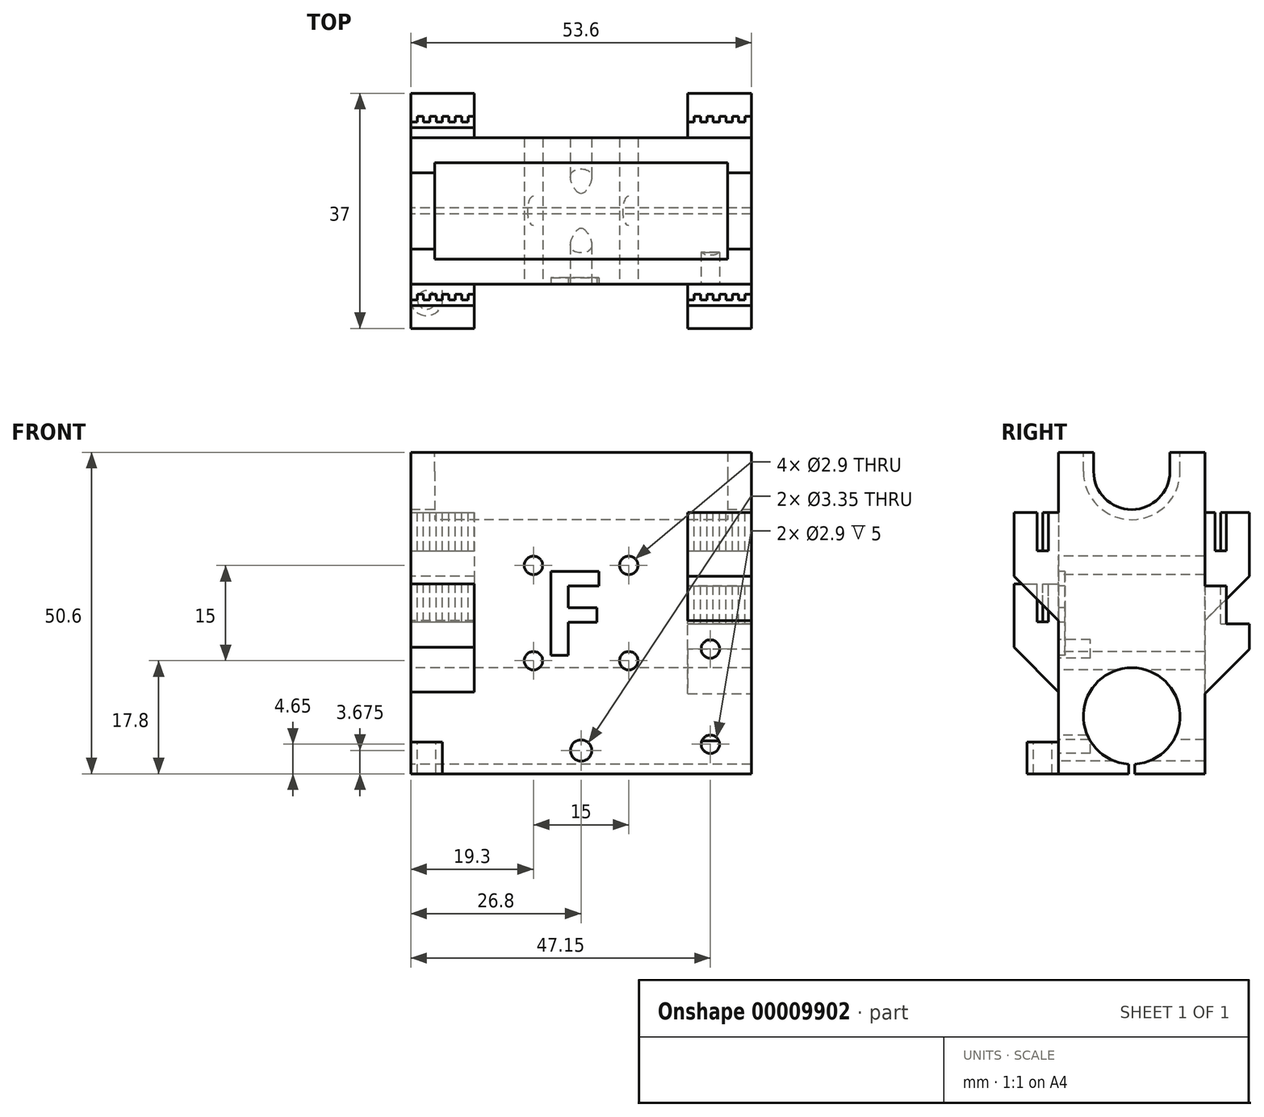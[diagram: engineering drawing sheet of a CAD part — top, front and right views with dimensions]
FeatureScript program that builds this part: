
annotation { "Feature Type Name" : "Feature", "Feature Type Description" : "" }
export const myFeature = defineFeature(function(context is Context, id is Id, definition is map)
    precondition{}
    {
        {
            assignVariable(context, id + "F0", {"name" : "LM8LUU", "anyValue" : 1.8});
        }
        {
            var Q0;
            Q0=qCreatedBy(makeId("Top.planeOp"),FACE);
            var sketch = newSketch(context, id + "F1", { "sketchPlane" : qUnion([Q0])});
            skLineSegment(sketch, "E0.bottom", {"start": v(0, 0) * mm, "end": v(53.6, 0) * mm});
            skLineSegment(sketch, "E0.top", {"start": v(0, 23) * mm, "end": v(53.6, 23) * mm});
            skLineSegment(sketch, "E0.left", {"start": v(0, 0) * mm, "end": v(0, 23) * mm});
            skLineSegment(sketch, "E0.right", {"start": v(53.6, 0) * mm, "end": v(53.6, 23) * mm});
            skSolve(sketch);
        }
        {
            var Q0;
            Q0 = qSketchRegion(id + "F1", true);
            extrude(context, id + "F2", {"entities" : qUnion([Q0]), "depth" : 50.6 * mm});
        }
        {
            var Q0;
            Q0=makeQuery(id+"F2.opExtrude","SWEPT_FACE",FACE,{"disambiguationData":[OSD([sQuery(id+"F1.wireOp",EDGE,"E0.left")])]});
            var sketch = newSketch(context, id + "F3", { "sketchPlane" : qUnion([Q0])});
            skCircle(sketch, "E1", {"center": v(-11.5, 9.1) * mm, "radius": 7.6 * mm});
            skCircle(sketch, "E2", {"center": v(-11.5, 47.6) * mm, "radius": 6 * mm});
            skLineSegment(sketch, "E3", {"start": v(-23, 47.6) * mm, "end": v(0, 47.6) * mm, "construction": true});
            skLineSegment(sketch, "E4", {"start": v(-17.5, 50.6) * mm, "end": v(-17.5, 47.6) * mm});
            skLineSegment(sketch, "E5", {"start": v(-5.5, 50.6) * mm, "end": v(-5.5, 47.6) * mm});
            skLineSegment(sketch, "E6", {"start": v(-23, 9.1) * mm, "end": v(0, 9.1) * mm, "construction": true});
            skLineSegment(sketch, "E7", {"start": v(-11.5, 9.1) * mm, "end": v(-11.5, 0) * mm, "construction": true});
            skLineSegment(sketch, "E8", {"start": v(-11.5, 0) * mm, "end": v(-12, 0) * mm});
            skLineSegment(sketch, "E9", {"start": v(-12, 0) * mm, "end": v(-12, 1.52) * mm});
            skLineSegment(sketch, "E10", {"start": v(-12, 1.52) * mm, "end": v(-11, 1.52) * mm});
            skLineSegment(sketch, "E11", {"start": v(-11, 1.52) * mm, "end": v(-11, 0) * mm});
            skLineSegment(sketch, "E12", {"start": v(-11, 0) * mm, "end": v(-11.5, 0) * mm});
            skLineSegment(sketch, "E13", {"start": v(-11.5, 15.6) * mm, "end": v(-11.5, 16.7) * mm});
            skLineSegment(sketch, "E14", {"start": v(-11.5, 15.6) * mm, "end": v(-7, 15.22) * mm});
            skLineSegment(sketch, "E15", {"start": v(-11.5, 15.6) * mm, "end": v(-16, 15.22) * mm});
            skCircle(sketch, "E16", {"center": v(-11.5, 47.6) * mm, "radius": 7.6 * mm});
            skLineSegment(sketch, "E17", {"start": v(-3.9, 47.6) * mm, "end": v(-3.9, 50.6) * mm});
            skLineSegment(sketch, "E18", {"start": v(-19.1, 47.6) * mm, "end": v(-19.1, 50.6) * mm});
            skSolve(sketch);
        }
        {
            var Q0;
            {var subQ0=sQuery(id+"F3.wireOp",EDGE,"E14");var subQ1=sQuery(id+"F3.wireOp",EDGE,"E1");var subQ3=makeQuery(id+"F3.imprint","INTERSECT",VERTEX,{"disambiguationData":[OD(0.0)],"derivedFrom":[subQ1,subQ0]});Q0=makeQuery(id+"F3.imprint","IMPRINT",FACE,{"disambiguationData":[TD([[makeQuery(id+"F3.imprint","IMPRINT",EDGE,{"disambiguationData":[TD([[subQ3,-1.0]])],"derivedFrom":subQ1}),1.0]])]});}
            var Q1;
            {var subQ0=sQuery(id+"F3.wireOp",EDGE,"E15");var subQ1=sQuery(id+"F3.wireOp",EDGE,"E1");var subQ3=makeQuery(id+"F3.imprint","INTERSECT",VERTEX,{"disambiguationData":[OD(0.0)],"derivedFrom":[subQ1,subQ0]});Q1=makeQuery(id+"F3.imprint","IMPRINT",FACE,{"disambiguationData":[TD([[makeQuery(id+"F3.imprint","IMPRINT",EDGE,{"disambiguationData":[TD([[subQ3,1.0]])],"derivedFrom":subQ1}),1.0]])]});}
            var Q2;
            Q2=makeQuery(id+"F3.imprint","IMPRINT",FACE,{"disambiguationData":[TD([[makeQuery(id+"F3.imprint","IMPRINT",EDGE,{"derivedFrom":sQuery(id+"F3.wireOp",EDGE,"E8")}),-1.0]])]});
            var Q3;
            {var subQ0=sQuery(id+"F3.wireOp",EDGE,"E10");Q3=makeQuery(id+"F3.imprint","IMPRINT",FACE,{"disambiguationData":[TD([[makeQuery(id+"F3.imprint","IMPRINT",EDGE,{"derivedFrom":subQ0}),-1.0]])]});}
            var Q4;
            {var subQ3=sQuery(id+"F3.wireOp",EDGE,"E13");Q4=makeQuery(id+"F3.imprint","IMPRINT",FACE,{"disambiguationData":[TD([[makeQuery(id+"F3.imprint","IMPRINT",EDGE,{"derivedFrom":subQ3}),-1.0]])]});}
            var Q5;
            {var subQ3=sQuery(id+"F3.wireOp",EDGE,"E13");Q5=makeQuery(id+"F3.imprint","IMPRINT",FACE,{"disambiguationData":[TD([[makeQuery(id+"F3.imprint","IMPRINT",EDGE,{"derivedFrom":subQ3}),1.0]])]});}
            var Q6;
            {var subQ7=sQuery(id+"F3.wireOp",EDGE,"E10");Q6=makeQuery(id+"F3.imprint","IMPRINT",FACE,{"disambiguationData":[TD([[makeQuery(id+"F3.imprint","IMPRINT",EDGE,{"derivedFrom":subQ7}),1.0]])]});}
            var Q7;
            {var subQ3=sQuery(id+"F3.wireOp",EDGE,"E5");Q7=makeQuery(id+"F3.imprint","IMPRINT",FACE,{"disambiguationData":[TD([[makeQuery(id+"F3.imprint","IMPRINT",EDGE,{"derivedFrom":subQ3}),-1.0]])]});}
            var Q8;
            {var subQ0=sQuery(id+"F3.wireOp",EDGE,"E4");Q8=makeQuery(id+"F3.imprint","IMPRINT",FACE,{"disambiguationData":[TD([[makeQuery(id+"F3.imprint","IMPRINT",EDGE,{"derivedFrom":subQ0}),1.0]])]});}
            var Q9;
            {var subQ0=sQuery(id+"F3.wireOp",EDGE,"E4");Q9=makeQuery(id+"F3.imprint","IMPRINT",FACE,{"disambiguationData":[TD([[makeQuery(id+"F3.imprint","IMPRINT",EDGE,{"derivedFrom":subQ0}),1.0]])]});}
            var Q10;
            {var subQ3=sQuery(id+"F3.wireOp",EDGE,"E5");Q10=makeQuery(id+"F3.imprint","IMPRINT",FACE,{"disambiguationData":[TD([[makeQuery(id+"F3.imprint","IMPRINT",EDGE,{"derivedFrom":subQ3}),-1.0]])]});}
            var Q11;
            {var subQ1=sQuery(id+"F3.wireOp",EDGE,"E2");var subQ4=makeQuery(id+"F3.imprint","INTERSECT",VERTEX,{"derivedFrom":[subQ1,sQuery(id+"F3.wireOp",EDGE,"E5")]});Q11=makeQuery(id+"F3.imprint","IMPRINT",FACE,{"disambiguationData":[TD([[makeQuery(id+"F3.imprint","IMPRINT",EDGE,{"disambiguationData":[TD([[subQ4,-1.0]])],"derivedFrom":subQ1}),1.0]])]});}
            extrude(context, id + "F4", {"entities" : qUnion([Q0, Q1, Q2, Q3, Q4, Q5, Q6, Q7, Q8, Q9, Q10, Q11]), "operationType" : NewBodyOperationType.REMOVE, "endBound" : BoundingType.THROUGH_ALL, "oppositeDirection" : true, "depth" : 25 * mm});
        }
        {
            var Q0;
            {var subQ3=sQuery(id+"F3.wireOp",EDGE,"E4");Q0=makeQuery(id+"F3.imprint","IMPRINT",FACE,{"disambiguationData":[TD([[makeQuery(id+"F3.imprint","IMPRINT",EDGE,{"derivedFrom":subQ3}),-1.0]])]});}
            var Q1;
            {var subQ3=sQuery(id+"F3.wireOp",EDGE,"E18");Q1=makeQuery(id+"F3.imprint","IMPRINT",FACE,{"disambiguationData":[TD([[makeQuery(id+"F3.imprint","IMPRINT",EDGE,{"derivedFrom":subQ3}),-1.0]])]});}
            var Q2;
            {var subQ3=sQuery(id+"F3.wireOp",EDGE,"E17");Q2=makeQuery(id+"F3.imprint","IMPRINT",FACE,{"disambiguationData":[TD([[makeQuery(id+"F3.imprint","IMPRINT",EDGE,{"derivedFrom":subQ3}),1.0]])]});}
            extrude(context, id + "F5", {"entities" : qUnion([Q0, Q1, Q2]), "operationType" : NewBodyOperationType.REMOVE, "oppositeDirection" : true, "depth" : (46.25 + getVariable(context, 'LM8LUU') * 2) * mm});
        }
        {
            var Q0;
            {var subQ3=sQuery(id+"F3.wireOp",EDGE,"E4");Q0=makeQuery(id+"F3.imprint","IMPRINT",FACE,{"disambiguationData":[TD([[makeQuery(id+"F3.imprint","IMPRINT",EDGE,{"derivedFrom":subQ3}),-1.0]])]});}
            var Q1;
            {var subQ3=sQuery(id+"F3.wireOp",EDGE,"E18");Q1=makeQuery(id+"F3.imprint","IMPRINT",FACE,{"disambiguationData":[TD([[makeQuery(id+"F3.imprint","IMPRINT",EDGE,{"derivedFrom":subQ3}),-1.0]])]});}
            var Q2;
            {var subQ3=sQuery(id+"F3.wireOp",EDGE,"E17");Q2=makeQuery(id+"F3.imprint","IMPRINT",FACE,{"disambiguationData":[TD([[makeQuery(id+"F3.imprint","IMPRINT",EDGE,{"derivedFrom":subQ3}),1.0]])]});}
            extrude(context, id + "F6", {"entities" : qUnion([Q0, Q1, Q2]), "operationType" : NewBodyOperationType.ADD, "oppositeDirection" : true, "depth" : (26.75 - getVariable(context, 'LM8LUU')) * mm});
        }
        {
            var Q0;
            {var subQ3=sQuery(id+"F3.wireOp",EDGE,"E4");Q0=makeQuery(id+"F3.imprint","IMPRINT",FACE,{"disambiguationData":[TD([[makeQuery(id+"F3.imprint","IMPRINT",EDGE,{"derivedFrom":subQ3}),-1.0]])]});}
            var Q1;
            {var subQ3=sQuery(id+"F3.wireOp",EDGE,"E18");Q1=makeQuery(id+"F3.imprint","IMPRINT",FACE,{"disambiguationData":[TD([[makeQuery(id+"F3.imprint","IMPRINT",EDGE,{"derivedFrom":subQ3}),-1.0]])]});}
            var Q2;
            {var subQ3=sQuery(id+"F3.wireOp",EDGE,"E17");Q2=makeQuery(id+"F3.imprint","IMPRINT",FACE,{"disambiguationData":[TD([[makeQuery(id+"F3.imprint","IMPRINT",EDGE,{"derivedFrom":subQ3}),1.0]])]});}
            extrude(context, id + "F7", {"entities" : qUnion([Q0, Q1, Q2]), "operationType" : NewBodyOperationType.REMOVE, "oppositeDirection" : true, "depth" : (23.25 + getVariable(context, 'LM8LUU')) * mm});
        }
        {
            var Q0;
            {var subQ3=sQuery(id+"F3.wireOp",EDGE,"E4");Q0=makeQuery(id+"F3.imprint","IMPRINT",FACE,{"disambiguationData":[TD([[makeQuery(id+"F3.imprint","IMPRINT",EDGE,{"derivedFrom":subQ3}),-1.0]])]});}
            var Q1;
            {var subQ3=sQuery(id+"F3.wireOp",EDGE,"E18");Q1=makeQuery(id+"F3.imprint","IMPRINT",FACE,{"disambiguationData":[TD([[makeQuery(id+"F3.imprint","IMPRINT",EDGE,{"derivedFrom":subQ3}),-1.0]])]});}
            var Q2;
            {var subQ3=sQuery(id+"F3.wireOp",EDGE,"E17");Q2=makeQuery(id+"F3.imprint","IMPRINT",FACE,{"disambiguationData":[TD([[makeQuery(id+"F3.imprint","IMPRINT",EDGE,{"derivedFrom":subQ3}),1.0]])]});}
            extrude(context, id + "F8", {"entities" : qUnion([Q0, Q1, Q2]), "operationType" : NewBodyOperationType.ADD, "oppositeDirection" : true, "depth" : 3.75 * mm});
        }
        {
            var Q0;
            Q0=makeQuery(id+"F2.opExtrude","SWEPT_FACE",FACE,{"disambiguationData":[OSD([sQuery(id+"F1.wireOp",EDGE,"E0.bottom")])]});
            var sketch = newSketch(context, id + "F9", { "sketchPlane" : qUnion([Q0])});
            skLineSegment(sketch, "E19.bottom", {"start": v(0, 29.9) * mm, "end": v(10, 29.9) * mm});
            skLineSegment(sketch, "E19.top", {"start": v(0, 9.9) * mm, "end": v(10, 9.9) * mm});
            skLineSegment(sketch, "E19.left", {"start": v(0, 29.9) * mm, "end": v(0, 9.9) * mm});
            skLineSegment(sketch, "E19.right", {"start": v(10, 29.9) * mm, "end": v(10, 9.9) * mm});
            skLineSegment(sketch, "E20.bottom", {"start": v(53.6, 41.1) * mm, "end": v(43.6, 41.1) * mm});
            skLineSegment(sketch, "E20.top", {"start": v(53.6, 21.1) * mm, "end": v(43.6, 21.1) * mm});
            skLineSegment(sketch, "E20.left", {"start": v(53.6, 41.1) * mm, "end": v(53.6, 21.1) * mm});
            skLineSegment(sketch, "E20.right", {"start": v(43.6, 41.1) * mm, "end": v(43.6, 21.1) * mm});
            skPoint(sketch, "E21", {"position": v(0, 47.6) * mm});
            skPoint(sketch, "E22", {"position": v(0, 9.4) * mm});
            skSolve(sketch);
        }
        {
            var Q0;
            Q0 = qSketchRegion(id + "F9", true);
            extrude(context, id + "F10", {"entities" : qUnion([Q0]), "operationType" : NewBodyOperationType.ADD, "depth" : 7 * mm});
        }
        {
            var Q0;
            Q0=makeQuery(id+"F10.opExtrude","CAP_EDGE",EDGE,{"disambiguationData":[OSD([sQuery(id+"F9.wireOp",EDGE,"E19.top")])],"isStart":false});
            var Q1;
            Q1=makeQuery(id+"F10.opExtrude","CAP_EDGE",EDGE,{"disambiguationData":[OSD([sQuery(id+"F9.wireOp",EDGE,"E20.top")])],"isStart":false});
            chamfer(context, id + "F11", {"entities" : qUnion([Q0, Q1]), "width" : 10 * mm, "tangentPropagation" : true});
        }
        {
            var Q0;
            Q0=makeQuery(id+"F10.opExtrude","SWEPT_FACE",FACE,{"disambiguationData":[OSD([sQuery(id+"F9.wireOp",EDGE,"E19.bottom")])]});
            var sketch = newSketch(context, id + "F12", { "sketchPlane" : qUnion([Q0])});
            skLineSegment(sketch, "E23", {"start": v(-935.9, 0) * mm, "end": v(-935.88, -4.54) * mm});
            skLineSegment(sketch, "E24.left", {"start": v(0, -3.4) * mm, "end": v(0, -1.6) * mm});
            skLineSegment(sketch, "E25", {"start": v(6, -2.5) * mm, "end": v(7, -2.5) * mm});
            skLineSegment(sketch, "E26", {"start": v(4, -2.5) * mm, "end": v(5, -2.5) * mm});
            skLineSegment(sketch, "E27", {"start": v(0, -2.5) * mm, "end": v(1, -2.5) * mm});
            skLineSegment(sketch, "E28", {"start": v(7, -1.6) * mm, "end": v(8, -1.6) * mm});
            skLineSegment(sketch, "E29", {"start": v(2, -2.5) * mm, "end": v(3, -2.5) * mm});
            skLineSegment(sketch, "E30", {"start": v(3, -1.6) * mm, "end": v(4, -1.6) * mm});
            skLineSegment(sketch, "E31", {"start": v(8, -2.5) * mm, "end": v(9, -2.5) * mm});
            skLineSegment(sketch, "E32", {"start": v(8, -1.6) * mm, "end": v(8, -2.5) * mm});
            skLineSegment(sketch, "E33", {"start": v(9, -2.5) * mm, "end": v(9, -1.6) * mm});
            skLineSegment(sketch, "E34", {"start": v(10, -1.6) * mm, "end": v(10, -2.5) * mm});
            skLineSegment(sketch, "E35", {"start": v(6, -1.6) * mm, "end": v(6, -2.5) * mm});
            skLineSegment(sketch, "E36", {"start": v(2, -1.6) * mm, "end": v(2, -2.5) * mm});
            skLineSegment(sketch, "E37", {"start": v(1, -1.6) * mm, "end": v(2, -1.6) * mm});
            skLineSegment(sketch, "E38", {"start": v(1, -2.5) * mm, "end": v(1, -1.6) * mm});
            skLineSegment(sketch, "E39", {"start": v(9, -1.6) * mm, "end": v(10, -1.6) * mm});
            skLineSegment(sketch, "E40", {"start": v(5, -1.6) * mm, "end": v(6, -1.6) * mm});
            skLineSegment(sketch, "E41", {"start": v(5, -2.5) * mm, "end": v(5, -1.6) * mm});
            skLineSegment(sketch, "E42", {"start": v(3, -2.5) * mm, "end": v(3, -1.6) * mm});
            skLineSegment(sketch, "E43", {"start": v(4, -1.6) * mm, "end": v(4, -2.5) * mm});
            skLineSegment(sketch, "E44", {"start": v(7, -2.5) * mm, "end": v(7, -1.6) * mm});
            skLineSegment(sketch, "E45", {"start": v(0, -1.6) * mm, "end": v(0, -2.5) * mm});
            skLineSegment(sketch, "E46", {"start": v(10, -2.5) * mm, "end": v(10, -3.4) * mm});
            skLineSegment(sketch, "E47", {"start": v(0, -3.4) * mm, "end": v(10, -3.4) * mm});
            skLineSegment(sketch, "E48", {"start": v(5.3, -1.6) * mm, "end": v(5.3, 0) * mm});
            skSolve(sketch);
        }
        {
            var Q0;
            Q0 = qSketchRegion(id + "F12", true);
            extrude(context, id + "F13", {"entities" : qUnion([Q0]), "operationType" : NewBodyOperationType.REMOVE, "oppositeDirection" : true, "depth" : 6 * mm});
        }
        {
            var Q0;
            Q0=makeQuery(id+"F10.opExtrude","SWEPT_FACE",FACE,{"disambiguationData":[OSD([sQuery(id+"F9.wireOp",EDGE,"E20.bottom")])]});
            var sketch = newSketch(context, id + "F14", { "sketchPlane" : qUnion([Q0])});
            skLineSegment(sketch, "E49.left", {"start": v(43.6, -3.4) * mm, "end": v(43.6, -1.6) * mm});
            skLineSegment(sketch, "E50", {"start": v(49.6, -2.5) * mm, "end": v(50.6, -2.5) * mm});
            skLineSegment(sketch, "E51", {"start": v(47.6, -2.5) * mm, "end": v(48.6, -2.5) * mm});
            skLineSegment(sketch, "E52", {"start": v(43.6, -2.5) * mm, "end": v(44.6, -2.5) * mm});
            skLineSegment(sketch, "E53", {"start": v(50.6, -1.6) * mm, "end": v(51.6, -1.6) * mm});
            skLineSegment(sketch, "E54", {"start": v(45.6, -2.5) * mm, "end": v(46.6, -2.5) * mm});
            skLineSegment(sketch, "E55", {"start": v(46.6, -1.6) * mm, "end": v(47.6, -1.6) * mm});
            skLineSegment(sketch, "E56", {"start": v(51.6, -2.5) * mm, "end": v(52.6, -2.5) * mm});
            skLineSegment(sketch, "E57", {"start": v(51.6, -1.6) * mm, "end": v(51.6, -2.5) * mm});
            skLineSegment(sketch, "E58", {"start": v(52.6, -2.5) * mm, "end": v(52.6, -1.6) * mm});
            skLineSegment(sketch, "E59", {"start": v(53.6, -1.6) * mm, "end": v(53.6, -2.5) * mm});
            skLineSegment(sketch, "E60", {"start": v(49.6, -1.6) * mm, "end": v(49.6, -2.5) * mm});
            skLineSegment(sketch, "E61", {"start": v(45.6, -1.6) * mm, "end": v(45.6, -2.5) * mm});
            skLineSegment(sketch, "E62", {"start": v(44.6, -1.6) * mm, "end": v(45.6, -1.6) * mm});
            skLineSegment(sketch, "E63", {"start": v(44.6, -2.5) * mm, "end": v(44.6, -1.6) * mm});
            skLineSegment(sketch, "E64", {"start": v(52.6, -1.6) * mm, "end": v(53.6, -1.6) * mm});
            skLineSegment(sketch, "E65", {"start": v(48.6, -1.6) * mm, "end": v(49.6, -1.6) * mm});
            skLineSegment(sketch, "E66", {"start": v(48.6, -2.5) * mm, "end": v(48.6, -1.6) * mm});
            skLineSegment(sketch, "E67", {"start": v(46.6, -2.5) * mm, "end": v(46.6, -1.6) * mm});
            skLineSegment(sketch, "E68", {"start": v(47.6, -1.6) * mm, "end": v(47.6, -2.5) * mm});
            skLineSegment(sketch, "E69", {"start": v(50.6, -2.5) * mm, "end": v(50.6, -1.6) * mm});
            skLineSegment(sketch, "E70", {"start": v(43.6, -1.6) * mm, "end": v(43.6, -2.5) * mm});
            skLineSegment(sketch, "E71", {"start": v(53.6, -2.5) * mm, "end": v(53.6, -3.4) * mm});
            skLineSegment(sketch, "E72", {"start": v(43.6, -3.4) * mm, "end": v(53.6, -3.4) * mm});
            skLineSegment(sketch, "E73", {"start": v(48.83, -1.6) * mm, "end": v(48.83, 0) * mm});
            skSolve(sketch);
        }
        {
            var Q0;
            Q0 = qSketchRegion(id + "F14", true);
            extrude(context, id + "F15", {"entities" : qUnion([Q0]), "operationType" : NewBodyOperationType.REMOVE, "oppositeDirection" : true, "depth" : 6 * mm});
        }
        {
            var Q0;
            Q0=makeQuery(id+"F2.opExtrude","SWEPT_FACE",FACE,{"disambiguationData":[OSD([sQuery(id+"F1.wireOp",EDGE,"E0.top")])]});
            var sketch = newSketch(context, id + "F16", { "sketchPlane" : qUnion([Q0])});
            skLineSegment(sketch, "E74.bottom", {"start": v(-53.6, 9.6) * mm, "end": v(-43.6, 9.6) * mm});
            skLineSegment(sketch, "E74.top", {"start": v(-53.6, 29.6) * mm, "end": v(-43.6, 29.6) * mm});
            skLineSegment(sketch, "E74.left", {"start": v(-53.6, 9.6) * mm, "end": v(-53.6, 29.6) * mm});
            skLineSegment(sketch, "E74.right", {"start": v(-43.6, 9.6) * mm, "end": v(-43.6, 29.6) * mm});
            skLineSegment(sketch, "E75.bottom", {"start": v(0, 41.1) * mm, "end": v(-10, 41.1) * mm});
            skLineSegment(sketch, "E75.top", {"start": v(0, 21.1) * mm, "end": v(-10, 21.1) * mm});
            skLineSegment(sketch, "E75.left", {"start": v(0, 41.1) * mm, "end": v(0, 21.1) * mm});
            skLineSegment(sketch, "E75.right", {"start": v(-10, 41.1) * mm, "end": v(-10, 21.1) * mm});
            skSolve(sketch);
        }
        {
            var Q0;
            Q0 = qSketchRegion(id + "F16", true);
            extrude(context, id + "F17", {"entities" : qUnion([Q0]), "operationType" : NewBodyOperationType.ADD, "depth" : 7 * mm});
        }
        {
            var Q0;
            Q0=makeQuery(id+"F17.opExtrude","SWEPT_FACE",FACE,{"disambiguationData":[OSD([sQuery(id+"F16.wireOp",EDGE,"E74.top")])]});
            var sketch = newSketch(context, id + "F18", { "sketchPlane" : qUnion([Q0])});
            skLineSegment(sketch, "E76.left", {"start": v(43.6, 24.6) * mm, "end": v(43.6, 26.4) * mm});
            skLineSegment(sketch, "E77", {"start": v(49.6, 25.5) * mm, "end": v(50.6, 25.5) * mm});
            skLineSegment(sketch, "E78", {"start": v(47.6, 25.5) * mm, "end": v(48.6, 25.5) * mm});
            skLineSegment(sketch, "E79", {"start": v(43.6, 25.5) * mm, "end": v(44.6, 25.5) * mm});
            skLineSegment(sketch, "E80", {"start": v(50.6, 26.4) * mm, "end": v(51.6, 26.4) * mm});
            skLineSegment(sketch, "E81", {"start": v(45.6, 25.5) * mm, "end": v(46.6, 25.5) * mm});
            skLineSegment(sketch, "E82", {"start": v(46.6, 26.4) * mm, "end": v(47.6, 26.4) * mm});
            skLineSegment(sketch, "E83", {"start": v(51.6, 25.5) * mm, "end": v(52.6, 25.5) * mm});
            skLineSegment(sketch, "E84", {"start": v(51.6, 26.4) * mm, "end": v(51.6, 25.5) * mm});
            skLineSegment(sketch, "E85", {"start": v(52.6, 25.5) * mm, "end": v(52.6, 26.4) * mm});
            skLineSegment(sketch, "E86", {"start": v(53.6, 26.4) * mm, "end": v(53.6, 25.5) * mm});
            skLineSegment(sketch, "E87", {"start": v(49.6, 26.4) * mm, "end": v(49.6, 25.5) * mm});
            skLineSegment(sketch, "E88", {"start": v(45.6, 26.4) * mm, "end": v(45.6, 25.5) * mm});
            skLineSegment(sketch, "E89", {"start": v(44.6, 26.4) * mm, "end": v(45.6, 26.4) * mm});
            skLineSegment(sketch, "E90", {"start": v(44.6, 25.5) * mm, "end": v(44.6, 26.4) * mm});
            skLineSegment(sketch, "E91", {"start": v(52.6, 26.4) * mm, "end": v(53.6, 26.4) * mm});
            skLineSegment(sketch, "E92", {"start": v(48.6, 26.4) * mm, "end": v(49.6, 26.4) * mm});
            skLineSegment(sketch, "E93", {"start": v(48.6, 25.5) * mm, "end": v(48.6, 26.4) * mm});
            skLineSegment(sketch, "E94", {"start": v(46.6, 25.5) * mm, "end": v(46.6, 26.4) * mm});
            skLineSegment(sketch, "E95", {"start": v(47.6, 26.4) * mm, "end": v(47.6, 25.5) * mm});
            skLineSegment(sketch, "E96", {"start": v(50.6, 25.5) * mm, "end": v(50.6, 26.4) * mm});
            skLineSegment(sketch, "E97", {"start": v(43.6, 26.4) * mm, "end": v(43.6, 25.5) * mm});
            skLineSegment(sketch, "E98", {"start": v(53.6, 25.5) * mm, "end": v(53.6, 24.6) * mm});
            skLineSegment(sketch, "E99", {"start": v(43.6, 24.6) * mm, "end": v(53.6, 24.6) * mm});
            skLineSegment(sketch, "E100", {"start": v(48.6, 24.6) * mm, "end": v(48.6, 23) * mm});
            skSolve(sketch);
        }
        {
            var Q0;
            {var subQ4=sQuery(id+"F18.wireOp",EDGE,"E76.left");Q0=makeQuery(id+"F18.imprint","IMPRINT",FACE,{"disambiguationData":[TD([[makeQuery(id+"F18.imprint","IMPRINT",EDGE,{"derivedFrom":subQ4}),1.0]])]});}
            extrude(context, id + "F19", {"entities" : qUnion([Q0]), "operationType" : NewBodyOperationType.REMOVE, "oppositeDirection" : true, "depth" : 6 * mm});
        }
        {
            var Q0;
            Q0=makeQuery(id+"F17.opExtrude","SWEPT_FACE",FACE,{"disambiguationData":[OSD([sQuery(id+"F16.wireOp",EDGE,"E75.bottom")])]});
            var sketch = newSketch(context, id + "F20", { "sketchPlane" : qUnion([Q0])});
            skLineSegment(sketch, "E101", {"start": v(6, 25.5) * mm, "end": v(7, 25.5) * mm});
            skLineSegment(sketch, "E102", {"start": v(4, 25.5) * mm, "end": v(5, 25.5) * mm});
            skLineSegment(sketch, "E103", {"start": v(0, 25.5) * mm, "end": v(1, 25.5) * mm});
            skLineSegment(sketch, "E104", {"start": v(7, 26.4) * mm, "end": v(8, 26.4) * mm});
            skLineSegment(sketch, "E105", {"start": v(2, 25.5) * mm, "end": v(3, 25.5) * mm});
            skLineSegment(sketch, "E106", {"start": v(3, 26.4) * mm, "end": v(4, 26.4) * mm});
            skLineSegment(sketch, "E107", {"start": v(8, 25.5) * mm, "end": v(9, 25.5) * mm});
            skLineSegment(sketch, "E108", {"start": v(8, 26.4) * mm, "end": v(8, 25.5) * mm});
            skLineSegment(sketch, "E109", {"start": v(9, 25.5) * mm, "end": v(9, 26.4) * mm});
            skLineSegment(sketch, "E110", {"start": v(10, 26.4) * mm, "end": v(10, 25.5) * mm});
            skLineSegment(sketch, "E111", {"start": v(6, 26.4) * mm, "end": v(6, 25.5) * mm});
            skLineSegment(sketch, "E112", {"start": v(2, 26.4) * mm, "end": v(2, 25.5) * mm});
            skLineSegment(sketch, "E113", {"start": v(1, 26.4) * mm, "end": v(2, 26.4) * mm});
            skLineSegment(sketch, "E114", {"start": v(1, 25.5) * mm, "end": v(1, 26.4) * mm});
            skLineSegment(sketch, "E115", {"start": v(9, 26.4) * mm, "end": v(10, 26.4) * mm});
            skLineSegment(sketch, "E116", {"start": v(5, 26.4) * mm, "end": v(6, 26.4) * mm});
            skLineSegment(sketch, "E117", {"start": v(5, 25.5) * mm, "end": v(5, 26.4) * mm});
            skLineSegment(sketch, "E118", {"start": v(3, 25.5) * mm, "end": v(3, 26.4) * mm});
            skLineSegment(sketch, "E119", {"start": v(4, 26.4) * mm, "end": v(4, 25.5) * mm});
            skLineSegment(sketch, "E120", {"start": v(7, 25.5) * mm, "end": v(7, 26.4) * mm});
            skLineSegment(sketch, "E121", {"start": v(10, 25.5) * mm, "end": v(10, 24.6) * mm});
            skLineSegment(sketch, "E122", {"start": v(0, 24.6) * mm, "end": v(10, 24.6) * mm});
            skLineSegment(sketch, "E123", {"start": v(5, 24.6) * mm, "end": v(5, 23) * mm});
            skLineSegment(sketch, "E124", {"start": v(0, 24.6) * mm, "end": v(0, 25.5) * mm});
            skSolve(sketch);
        }
        {
            var Q0;
            Q0=makeQuery(id+"F20.imprint","IMPRINT",FACE,{"disambiguationData":[TD([[makeQuery(id+"F20.imprint","IMPRINT",EDGE,{"derivedFrom":sQuery(id+"F20.wireOp",EDGE,"E101")}),-1.0]])]});
            extrude(context, id + "F21", {"entities" : qUnion([Q0]), "operationType" : NewBodyOperationType.REMOVE, "oppositeDirection" : true, "depth" : 6 * mm});
        }
        {
            var Q0;
            Q0=makeQuery(id+"F17.opExtrude","CAP_EDGE",EDGE,{"disambiguationData":[OSD([sQuery(id+"F16.wireOp",EDGE,"E75.top")])],"isStart":false});
            var Q1;
            Q1=makeQuery(id+"F17.opExtrude","CAP_EDGE",EDGE,{"disambiguationData":[OSD([sQuery(id+"F16.wireOp",EDGE,"E74.bottom")])],"isStart":false});
            chamfer(context, id + "F22", {"entities" : qUnion([Q0, Q1]), "width" : 10 * mm, "tangentPropagation" : true});
        }
        {
            var Q0;
            Q0=makeQuery(id+"F2.opExtrude","SWEPT_FACE",FACE,{"disambiguationData":[OSD([sQuery(id+"F1.wireOp",EDGE,"E0.bottom")])]});
            var sketch = newSketch(context, id + "F23", { "sketchPlane" : qUnion([Q0])});
            skCircle(sketch, "E125", {"center": v(19.3, 32.8) * mm, "radius": 1.45 * mm});
            skCircle(sketch, "E126", {"center": v(34.3, 32.8) * mm, "radius": 1.45 * mm});
            skCircle(sketch, "E127", {"center": v(19.3, 17.8) * mm, "radius": 1.45 * mm});
            skCircle(sketch, "E128", {"center": v(34.3, 17.8) * mm, "radius": 1.45 * mm});
            skLineSegment(sketch, "E129", {"start": v(19.3, 32.8) * mm, "end": v(0, 32.8) * mm});
            skLineSegment(sketch, "E130", {"start": v(34.3, 17.8) * mm, "end": v(53.6, 17.8) * mm});
            skLineSegment(sketch, "E131", {"start": v(34.3, 32.8) * mm, "end": v(34.3, 50.6) * mm});
            skLineSegment(sketch, "E132", {"start": v(19.3, 17.8) * mm, "end": v(19.3, 0) * mm});
            skCircle(sketch, "E133", {"center": v(26.8, 3.68) * mm, "radius": 1.68 * mm});
            skLineSegment(sketch, "E134", {"start": v(26.8, 0) * mm, "end": v(26.8, 13.82) * mm, "construction": true});
            skSolve(sketch);
        }
        {
            var Q0;
            Q0 = qSketchRegion(id + "F23", true);
            var Q1;
            Q1=makeQuery(id+"F23.imprint","IMPRINT",FACE,{"disambiguationData":[TD([[makeQuery(id+"F23.imprint","IMPRINT",EDGE,{"derivedFrom":sQuery(id+"F23.wireOp",EDGE,"E125")}),1.0]])]});
            var Q2;
            Q2=makeQuery(id+"F23.imprint","IMPRINT",FACE,{"disambiguationData":[TD([[makeQuery(id+"F23.imprint","IMPRINT",EDGE,{"derivedFrom":sQuery(id+"F23.wireOp",EDGE,"E126")}),1.0]])]});
            var Q3;
            Q3=makeQuery(id+"F23.imprint","IMPRINT",FACE,{"disambiguationData":[TD([[makeQuery(id+"F23.imprint","IMPRINT",EDGE,{"derivedFrom":sQuery(id+"F23.wireOp",EDGE,"E128")}),1.0]])]});
            var Q4;
            Q4=makeQuery(id+"F23.imprint","IMPRINT",FACE,{"disambiguationData":[TD([[makeQuery(id+"F23.imprint","IMPRINT",EDGE,{"derivedFrom":sQuery(id+"F23.wireOp",EDGE,"E127")}),1.0]])]});
            extrude(context, id + "F24", {"entities" : qUnion([Q0, Q1, Q2, Q3, Q4]), "operationType" : NewBodyOperationType.REMOVE, "endBound" : BoundingType.THROUGH_ALL, "oppositeDirection" : true, "depth" : 25 * mm});
        }
        {
            var Q0;
            Q0=makeQuery(id+"F2.opExtrude","SWEPT_FACE",FACE,{"disambiguationData":[OSD([sQuery(id+"F1.wireOp",EDGE,"E0.bottom")])]});
            var sketch = newSketch(context, id + "F25", { "sketchPlane" : qUnion([Q0])});
            skCircle(sketch, "E135", {"center": v(47.15, 19.65) * mm, "radius": 1.45 * mm});
            skCircle(sketch, "E136", {"center": v(47.15, 4.65) * mm, "radius": 1.45 * mm});
            skSolve(sketch);
        }
        {
            var Q0;
            Q0 = qSketchRegion(id + "F25", true);
            extrude(context, id + "F26", {"entities" : qUnion([Q0]), "operationType" : NewBodyOperationType.REMOVE, "oppositeDirection" : true, "depth" : 5 * mm});
        }
        {
            var Q0;
            Q0=makeQuery(id+"F2.opExtrude","SWEPT_FACE",FACE,{"disambiguationData":[OSD([sQuery(id+"F1.wireOp",EDGE,"E0.bottom")])]});
            var sketch = newSketch(context, id + "F27", { "sketchPlane" : qUnion([Q0])});
            skText(sketch, "E137", { "text": "F", "fontName": "OpenSans-Bold.ttf"});
            skLineSegment(sketch, "E138", {"start": v(19.3, 32.8) * mm, "end": v(19.3, 17.8) * mm, "construction": true});
            skLineSegment(sketch, "E139", {"start": v(19.3, 17.8) * mm, "end": v(34.3, 17.8) * mm, "construction": true});
            skLineSegment(sketch, "E140", {"start": v(34.3, 17.8) * mm, "end": v(34.3, 32.8) * mm, "construction": true});
            skLineSegment(sketch, "E141", {"start": v(34.3, 32.8) * mm, "end": v(19.3, 32.8) * mm, "construction": true});
            skLineSegment(sketch, "E142", {"start": v(19.3, 25.3) * mm, "end": v(22.2, 25.3) * mm, "construction": true});
            skLineSegment(sketch, "E143", {"start": v(31.4, 25.3) * mm, "end": v(34.3, 25.3) * mm, "construction": true});
            skLineSegment(sketch, "E144", {"start": v(26.8, 18.66) * mm, "end": v(26.8, 17.8) * mm, "construction": true});
            skLineSegment(sketch, "E145", {"start": v(26.8, 32.8) * mm, "end": v(26.8, 31.94) * mm, "construction": true});
            const initialGuessF27  = {"E137": [0.0204, 0.01866, 1, 0, 0.01328]};
            skSetInitialGuess(sketch, initialGuessF27);
            skSolve(sketch);
        }
        {
            var Q0;
            Q0 = qSketchRegion(id + "F27", true);
            extrude(context, id + "F28", {"entities" : qUnion([Q0]), "operationType" : NewBodyOperationType.REMOVE, "oppositeDirection" : true, "depth" : 1 * mm});
        }
        {
            var Q0;
            Q0=makeQuery(id+"F2.opExtrude","SWEPT_FACE",FACE,{"disambiguationData":[OSD([sQuery(id+"F1.wireOp",EDGE,"E0.bottom")])]});
            var sketch = newSketch(context, id + "F29", { "sketchPlane" : qUnion([Q0])});
            skLineSegment(sketch, "E146.bottom", {"start": v(0, 0) * mm, "end": v(5, 0) * mm});
            skLineSegment(sketch, "E146.top", {"start": v(0, 5) * mm, "end": v(5, 5) * mm});
            skLineSegment(sketch, "E146.left", {"start": v(0, 0) * mm, "end": v(0, 5) * mm});
            skLineSegment(sketch, "E146.right", {"start": v(5, 0) * mm, "end": v(5, 5) * mm});
            skSolve(sketch);
        }
        {
            var Q0;
            Q0 = qSketchRegion(id + "F29", true);
            extrude(context, id + "F30", {"entities" : qUnion([Q0]), "operationType" : NewBodyOperationType.ADD, "depth" : 5 * mm});
        }
        {
            var Q0;
            Q0=makeQuery(id+"F30.opExtrude","SWEPT_FACE",FACE,{"disambiguationData":[OSD([sQuery(id+"F29.wireOp",EDGE,"E146.top")])]});
            var sketch = newSketch(context, id + "F31", { "sketchPlane" : qUnion([Q0])});
            skCircle(sketch, "E147", {"center": v(2.5, -2.5) * mm, "radius": 1.45 * mm});
            skLineSegment(sketch, "E148", {"start": v(0, -2.5) * mm, "end": v(5, -2.5) * mm});
            skSolve(sketch);
        }
        {
            var Q0;
            Q0 = qSketchRegion(id + "F31", true);
            extrude(context, id + "F32", {"entities" : qUnion([Q0]), "operationType" : NewBodyOperationType.REMOVE, "oppositeDirection" : true, "depth" : 25 * mm});
        }
        {
            var Q0;
            Q0=makeQuery(id+"F30.opExtrude","CAP_EDGE",EDGE,{"disambiguationData":[OSD([sQuery(id+"F29.wireOp",EDGE,"E146.left")])],"isStart":false});
            var Q1;
            Q1=makeQuery(id+"F30.opExtrude","CAP_EDGE",EDGE,{"disambiguationData":[OSD([sQuery(id+"F29.wireOp",EDGE,"E146.right")])],"isStart":false});
            fillet(context, id + "F33", {"entities" : qUnion([Q0, Q1]), "radius" : 2.5 * mm, "tangentPropagation" : true, "allowEdgeOverflow" : false});
        }
    });
